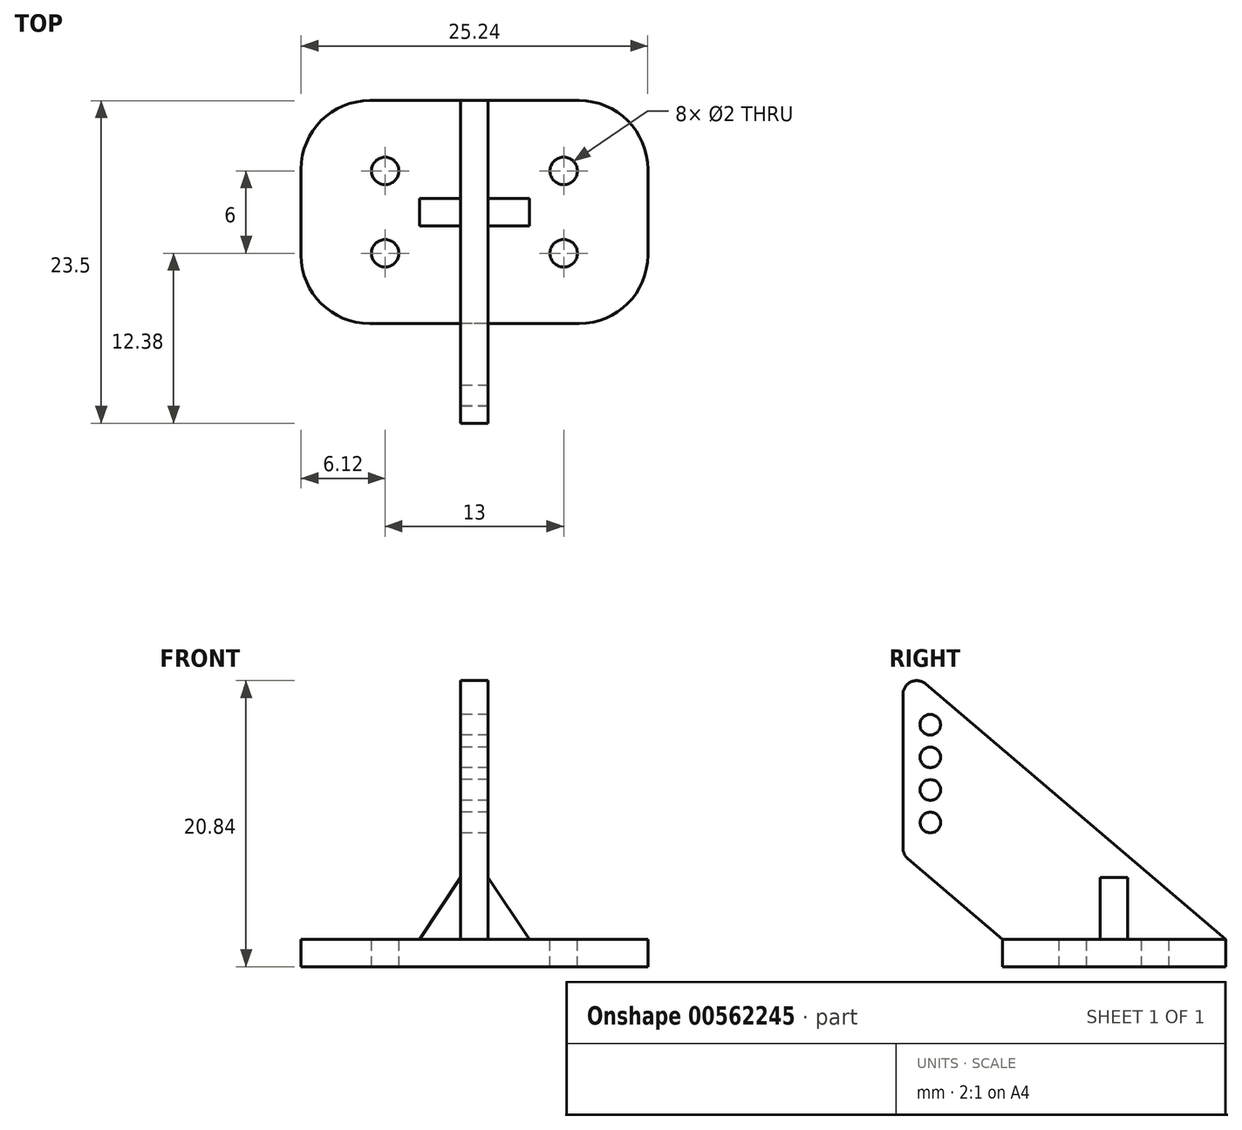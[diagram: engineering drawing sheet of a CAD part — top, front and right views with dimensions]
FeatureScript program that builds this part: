
annotation { "Feature Type Name" : "Feature", "Feature Type Description" : "" }
export const myFeature = defineFeature(function(context is Context, id is Id, definition is map)
    precondition{}
    {
        {
            var Q0;
            Q0=qCreatedBy(makeId("Top.planeOp"),FACE);
            var sketch = newSketch(context, id + "F0", { "sketchPlane" : qUnion([Q0])});
            skLineSegment(sketch, "E0.bottom", {"start": v(7.63, -8.12) * mm, "end": v(6.5, -8.12) * mm});
            skLineSegment(sketch, "E0.top", {"start": v(7.63, 8.12) * mm, "end": v(6.5, 8.12) * mm});
            skLineSegment(sketch, "E0.left", {"start": v(12.62, -3.12) * mm, "end": v(12.62, -3) * mm});
            skLineSegment(sketch, "E0.right", {"start": v(-12.62, -3.13) * mm, "end": v(-12.62, -3) * mm});
            skPoint(sketch, "E0.middle", {"position": v(0, 0) * mm});
            skLineSegment(sketch, "E1", {"start": v(-6.5, 8.12) * mm, "end": v(-7.63, 8.12) * mm});
            skLineSegment(sketch, "E2", {"start": v(6.5, 8.12) * mm, "end": v(1, 8.12) * mm});
            skLineSegment(sketch, "E3", {"start": v(-6.5, -8.12) * mm, "end": v(-7.63, -8.12) * mm});
            skLineSegment(sketch, "E4", {"start": v(6.5, -8.12) * mm, "end": v(1, -8.12) * mm});
            skLineSegment(sketch, "E5", {"start": v(12.62, -3) * mm, "end": v(12.62, -1) * mm});
            skLineSegment(sketch, "E6", {"start": v(12.62, 3) * mm, "end": v(12.62, 3.13) * mm});
            skLineSegment(sketch, "E7", {"start": v(-12.62, 3) * mm, "end": v(-12.62, 3.12) * mm});
            skLineSegment(sketch, "E8", {"start": v(-12.62, -3) * mm, "end": v(-12.62, -1) * mm});
            skLineSegment(sketch, "E9", {"start": v(-6.5, 8.12) * mm, "end": v(-6.5, -8.12) * mm, "construction": true});
            skLineSegment(sketch, "E10", {"start": v(6.5, 8.12) * mm, "end": v(6.5, -8.12) * mm, "construction": true});
            skLineSegment(sketch, "E11", {"start": v(12.62, 3) * mm, "end": v(-12.62, 3) * mm, "construction": true});
            skLineSegment(sketch, "E12", {"start": v(-12.62, -3) * mm, "end": v(12.62, -3) * mm, "construction": true});
            skCircle(sketch, "E13", {"center": v(-6.5, 3) * mm, "radius": 1 * mm});
            skCircle(sketch, "E14", {"center": v(-6.5, -3) * mm, "radius": 1 * mm});
            skCircle(sketch, "E15", {"center": v(6.5, 3) * mm, "radius": 1 * mm});
            skCircle(sketch, "E16", {"center": v(6.5, -3) * mm, "radius": 1 * mm});
            skPoint(sketch, "E17.visualSharp", {"position": v(-12.63, 8.12) * mm});
            skArc(sketch, "E17.filletArc", {"start": v(-7.63, 8.12) * mm, "mid": v(-11.16, 6.66) * mm, "end": v(-12.63, 3.13) * mm});
            skPoint(sketch, "E18.visualSharp", {"position": v(-12.62, -8.13) * mm});
            skArc(sketch, "E18.filletArc", {"start": v(-12.62, -3.13) * mm, "mid": v(-11.16, -6.66) * mm, "end": v(-7.63, -8.13) * mm});
            skPoint(sketch, "E19.visualSharp", {"position": v(12.62, -8.12) * mm});
            skArc(sketch, "E19.filletArc", {"start": v(7.63, -8.12) * mm, "mid": v(11.16, -6.66) * mm, "end": v(12.62, -3.12) * mm});
            skPoint(sketch, "E20.visualSharp", {"position": v(12.62, 8.12) * mm});
            skArc(sketch, "E20.filletArc", {"start": v(12.62, 3.13) * mm, "mid": v(11.16, 6.66) * mm, "end": v(7.63, 8.12) * mm});
            skLineSegment(sketch, "E21", {"start": v(-1, 8.12) * mm, "end": v(-1, -8.13) * mm});
            skLineSegment(sketch, "E22", {"start": v(1, 8.12) * mm, "end": v(1, -8.13) * mm});
            skLineSegment(sketch, "E23", {"start": v(-1, 8.12) * mm, "end": v(-6.5, 8.12) * mm});
            skLineSegment(sketch, "E24", {"start": v(1, 8.12) * mm, "end": v(-1, 8.12) * mm});
            skLineSegment(sketch, "E25", {"start": v(-1, -8.12) * mm, "end": v(-6.5, -8.12) * mm});
            skLineSegment(sketch, "E26", {"start": v(1, -8.12) * mm, "end": v(-1, -8.12) * mm});
            skLineSegment(sketch, "E27", {"start": v(-12.63, 1) * mm, "end": v(-12.63, 1) * mm});
            skLineSegment(sketch, "E28", {"start": v(-12.63, -1) * mm, "end": v(-4, -1) * mm, "construction": true});
            skLineSegment(sketch, "E29", {"start": v(-12.63, 1) * mm, "end": v(-4, 1) * mm, "construction": true});
            skLineSegment(sketch, "E30", {"start": v(-12.62, -1) * mm, "end": v(-12.62, 1) * mm});
            skLineSegment(sketch, "E31", {"start": v(12.62, 1) * mm, "end": v(12.62, 3) * mm});
            skLineSegment(sketch, "E32", {"start": v(12.62, -1) * mm, "end": v(12.62, 1) * mm});
            skLineSegment(sketch, "E33", {"start": v(-12.62, 1) * mm, "end": v(-12.62, 3) * mm});
            skLineSegment(sketch, "E34", {"start": v(-4, 1) * mm, "end": v(-4, 1) * mm});
            skLineSegment(sketch, "E35", {"start": v(4, 1) * mm, "end": v(4, -1) * mm});
            skLineSegment(sketch, "E36", {"start": v(-4, 1) * mm, "end": v(-4, -1) * mm});
            skLineSegment(sketch, "E37", {"start": v(4, 1) * mm, "end": v(12.62, 1) * mm, "construction": true});
            skLineSegment(sketch, "E38", {"start": v(4, -1) * mm, "end": v(12.62, -1) * mm, "construction": true});
            skLineSegment(sketch, "E39", {"start": v(-4, -1) * mm, "end": v(4, -1) * mm});
            skLineSegment(sketch, "E40", {"start": v(-4, 1) * mm, "end": v(4, 1) * mm});
            skSolve(sketch);
        }
        {
            var Q0;
            Q0=makeQuery(id+"F0.imprint","IMPRINT",FACE,{"disambiguationData":[TD([[makeQuery(id+"F0.imprint","IMPRINT",EDGE,{"derivedFrom":sQuery(id+"F0.wireOp",EDGE,"E0.bottom")}),-1.0]])]});
            var Q1;
            Q1=makeQuery(id+"F0.imprint","IMPRINT",FACE,{"disambiguationData":[TD([[makeQuery(id+"F0.imprint","IMPRINT",EDGE,{"derivedFrom":sQuery(id+"F0.wireOp",EDGE,"E0.right")}),-1.0]])]});
            var Q2;
            {var subQ0=sQuery(id+"F0.wireOp",EDGE,"E40");var subQ1=sQuery(id+"F0.wireOp",EDGE,"E21");var subQ2=makeQuery(id+"F0.imprint","INTERSECT",VERTEX,{"derivedFrom":[subQ1,subQ0]});Q2=makeQuery(id+"F0.imprint","IMPRINT",FACE,{"disambiguationData":[TD([[makeQuery(id+"F0.imprint","IMPRINT",EDGE,{"disambiguationData":[TD([[subQ2,-1.0]])],"derivedFrom":subQ1}),1.0]])]});}
            var Q3;
            {var subQ0=sQuery(id+"F0.wireOp",EDGE,"E24");Q3=makeQuery(id+"F0.imprint","IMPRINT",FACE,{"disambiguationData":[TD([[makeQuery(id+"F0.imprint","IMPRINT",EDGE,{"derivedFrom":subQ0}),1.0]])]});}
            var Q4;
            {var subQ0=sQuery(id+"F0.wireOp",EDGE,"E26");Q4=makeQuery(id+"F0.imprint","IMPRINT",FACE,{"disambiguationData":[TD([[makeQuery(id+"F0.imprint","IMPRINT",EDGE,{"derivedFrom":subQ0}),-1.0]])]});}
            var Q5;
            {var subQ5=sQuery(id+"F0.wireOp",EDGE,"E35");Q5=makeQuery(id+"F0.imprint","IMPRINT",FACE,{"disambiguationData":[TD([[makeQuery(id+"F0.imprint","IMPRINT",EDGE,{"derivedFrom":subQ5}),-1.0]])]});}
            var Q6;
            {var subQ5=sQuery(id+"F0.wireOp",EDGE,"E36");Q6=makeQuery(id+"F0.imprint","IMPRINT",FACE,{"disambiguationData":[TD([[makeQuery(id+"F0.imprint","IMPRINT",EDGE,{"derivedFrom":subQ5}),1.0]])]});}
            extrude(context, id + "F1", {"entities" : qUnion([Q0, Q1, Q2, Q3, Q4, Q5, Q6]), "oppositeDirection" : true, "depth" : 2 * mm, "offsetDistance" : 25 * mm});
        }
        {
            var Q0;
            Q0=qCreatedBy(makeId("Right.planeOp"),FACE);
            var sketch = newSketch(context, id + "F2", { "sketchPlane" : qUnion([Q0])});
            skLineSegment(sketch, "E41", {"start": v(0, 0) * mm, "end": v(0, 20) * mm, "construction": true});
            skLineSegment(sketch, "E42", {"start": v(0, 0) * mm, "end": v(8.12, 0) * mm});
            skLineSegment(sketch, "E43", {"start": v(0, 0) * mm, "end": v(-8.12, 0) * mm});
            skLineSegment(sketch, "E44.0", {"start": v(8.12, 0) * mm, "end": v(-8.13, 0) * mm});
            skLineSegment(sketch, "E45", {"start": v(8.12, 0) * mm, "end": v(-13.38, 0) * mm, "construction": true});
            skLineSegment(sketch, "E46", {"start": v(-15.38, 0) * mm, "end": v(-15.38, 20) * mm, "construction": true});
            skLineSegment(sketch, "E47", {"start": v(-13.73, 18.6) * mm, "end": v(8.12, 0) * mm});
            skLineSegment(sketch, "E48", {"start": v(-8.12, 0) * mm, "end": v(-15.02, 5.87) * mm});
            skLineSegment(sketch, "E49", {"start": v(-15.38, 17.84) * mm, "end": v(-15.38, 6.63) * mm});
            skLineSegment(sketch, "E50", {"start": v(-13.38, 0) * mm, "end": v(-15.38, 0) * mm, "construction": true});
            skLineSegment(sketch, "E51", {"start": v(-13.38, 0) * mm, "end": v(-13.38, 8.5) * mm, "construction": true});
            skLineSegment(sketch, "E52", {"start": v(-13.38, 8.5) * mm, "end": v(-13.38, 18.3) * mm, "construction": true});
            skCircle(sketch, "E53", {"center": v(-13.38, 8.5) * mm, "radius": 0.75 * mm});
            skCircle(sketch, "E54.1.0.0", {"center": v(-13.38, 10.87) * mm, "radius": 0.75 * mm});
            skCircle(sketch, "E54.2.0.0", {"center": v(-13.38, 13.25) * mm, "radius": 0.75 * mm});
            skCircle(sketch, "E54.3.0.0", {"center": v(-13.39, 15.62) * mm, "radius": 0.75 * mm});
            skLineSegment(sketch, "E54.direction1", {"start": v(-13.38, 8.5) * mm, "end": v(-13.38, 10.87) * mm, "construction": true});
            skPoint(sketch, "E55.visualSharp", {"position": v(-15.38, 20) * mm});
            skArc(sketch, "E55.filletArc", {"start": v(-13.73, 18.6) * mm, "mid": v(-14.8, 18.74) * mm, "end": v(-15.38, 17.84) * mm});
            skPoint(sketch, "E56.visualSharp", {"position": v(-15.38, 6.17) * mm});
            skArc(sketch, "E56.filletArc", {"start": v(-15.38, 6.63) * mm, "mid": v(-15.28, 6.21) * mm, "end": v(-15.02, 5.87) * mm});
            skSolve(sketch);
        }
        {
            var Q0;
            {var subQ1=sQuery(id+"F2.wireOp",EDGE,"E47");Q0=makeQuery(id+"F2.imprint","IMPRINT",FACE,{"disambiguationData":[TD([[makeQuery(id+"F2.imprint","IMPRINT",EDGE,{"derivedFrom":subQ1}),-1.0]])]});}
            extrude(context, id + "F3", {"entities" : qUnion([Q0]), "endBound" : BoundingType.SYMMETRIC, "depth" : 2 * mm, "offsetDistance" : 25 * mm});
        }
        {
            var Q0;
            Q0=qCreatedBy(makeId("Front.planeOp"),FACE);
            var sketch = newSketch(context, id + "F4", { "sketchPlane" : qUnion([Q0])});
            skLineSegment(sketch, "E57.0.1", {"start": v(1, 0) * mm, "end": v(4, 0) * mm});
            skLineSegment(sketch, "E57.0.3", {"start": v(4, 0) * mm, "end": v(1, 0) * mm});
            skLineSegment(sketch, "E57.1.1", {"start": v(-1, 0) * mm, "end": v(-4, 0) * mm});
            skLineSegment(sketch, "E57.1.3", {"start": v(-4, 0) * mm, "end": v(-1, 0) * mm});
            skLineSegment(sketch, "E58", {"start": v(1, 0) * mm, "end": v(1, 4.5) * mm});
            skLineSegment(sketch, "E59", {"start": v(1, 4.5) * mm, "end": v(-1, 4.5) * mm, "construction": true});
            skLineSegment(sketch, "E60", {"start": v(-1, 4.5) * mm, "end": v(-1, 0) * mm});
            skLineSegment(sketch, "E61", {"start": v(4, 0) * mm, "end": v(1, 4.5) * mm});
            skLineSegment(sketch, "E62", {"start": v(-1, 4.5) * mm, "end": v(-4, 0) * mm});
            skSolve(sketch);
        }
        {
            var Q0;
            Q0=makeQuery(id+"F4.imprint","IMPRINT",FACE,{"disambiguationData":[TD([[makeQuery(id+"F4.imprint","IMPRINT",EDGE,{"derivedFrom":sQuery(id+"F4.wireOp",EDGE,"E57.1.3")}),1.0]])]});
            var Q1;
            Q1 = qSketchRegion(id + "F4", true);
            extrude(context, id + "F5", {"entities" : qUnion([Q0, Q1]), "endBound" : BoundingType.SYMMETRIC, "depth" : 2 * mm, "offsetDistance" : 25 * mm});
        }
    });
